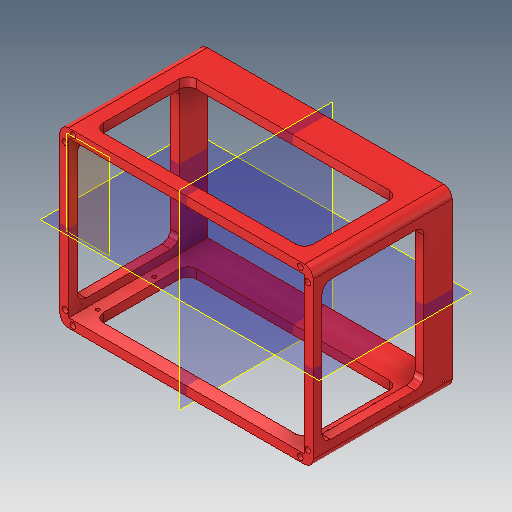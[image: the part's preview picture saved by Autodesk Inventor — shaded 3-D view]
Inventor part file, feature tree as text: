
AUTODESK INVENTOR PART (.ipt)
format: ipt  version: 2019.4 (Build 234330000, 330)  size: 421,376 bytes
history: native  units: mm
features: sketch x9, other x9, extrude x8, plane x6, reference x6, projected_geometry x5, fillet x1, hole x1
ambient origin geometry x8: Origin, YZ Plane, XZ Plane, XY Plane, X Axis, Y Axis, Z Axis, Center Point
bodies: Volumenkörper1 (feature_tree)
feature tree (45):
  plane  "Arbeitsebene1"
  extrude  "Extrusion1"  Depth=4.0mm TaperAngle=0.0deg
  sketch  "Skizze3"  dims[d16=4.1mm d17=64.1mm d18=0.0mm]
  plane  "Arbeitsebene2"
  plane  "Arbeitsebene3"
  plane  "Arbeitsebene4"
  extrude  "Extrusion2"  Depth=64.1mm TaperAngle=0.0deg
  extrude  "Extrusion3"  Depth=4.0mm
  extrude  "Extrusion4"  Depth=4.0mm
  fillet  "Rundung1"  Radius=3.0mm
  hole  "Bohrung2"  [1 undecoded]
  extrude  "Extrusion5"  Depth=105.0mm
  extrude  "Extrusion6"  Depth=10.0mm TaperAngle=0.0deg
  extrude  "Extrusion7"  Depth=10.0mm
  plane  "Work Plane5"
  plane  "Work Plane6"
  extrude  "Extrusion8"  Depth=10.0mm
  sketch  "Skizze1"  dims[d0=4.5mm d1=4.0mm d2=0.0mm]
  reference  "Referenz1"
  reference  "Referenz2"
  reference  "Referenz3"
  reference  "Referenz4"
  projected_geometry  "Projizierte Kontur1"
  sketch  "Skizze4"  dims[d20=3.0mm d21=0.0mm d22=4.0mm]
  projected_geometry  "Projizierte Kontur2"
  sketch  "Skizze5"  dims[d23=8.0mm d24=4.0mm d25=3.0mm d26=0.0mm]
  projected_geometry  "Projizierte Kontur3"
  sketch  "Skizze6"  dims[d27=4.0mm d28=112.0mm]
  sketch  "Skizze7"  dims[d29=67.0mm d30=105.0mm]
  sketch  "Skizze8"  dims[d31=76.0mm]
  reference  "Referenz7"
  projected_geometry  "Projizierte Kontur5"
  sketch  "Sketch9"  dims[d32=2.7mm d33=6.0mm d34=6.0mm d35=2.0mm d36=90.0deg d37=12.0mm d38=20.594885mm d39=10.0mm d40=0.0mm]
  projected_geometry  "Projected Loop6"
  sketch  "Sketch10"  dims[d41=1.8mm d42=1.8mm d43=2.5mm d44=2.5mm d45=10.0mm d46=0.0mm d47=2.8mm d48=2.8mm d49=2.8mm d50=2.8mm d51=4.0mm d52=0.0mm d53=80.0mm d54=71.0mm d55=108.0mm d56=4.1mm d57=71.8mm d58=108.8mm d59=54.4mm d60=71.8mm d61=35.9mm d62=10.0mm d63=0.0mm]
  reference  "Reference9"
  other  "Full_HITscope_v0.iam"
  other  "Assembly_Omniscope_v1:11"
  other  "02_Camera_Lid:1"
  other  "Assembly_Omniscope_v1:12"
  other  "Assembly_Omniscope_v1:2"
  other  "Assembly_Omniscope_v1:1"
  other  "07_Omnivision_Lamp_arm:1"
  other  "00_Microlinearmotor:1"
  other  "<userpath>\Documents\Inventor\HITscope\Full_HITscope_v0.iam"
note: 1 required parameter value undecoded (feature->parameter linkage not recoverable at this tier; creation-order binding heuristic only, values carry confidence <= 0.55)
